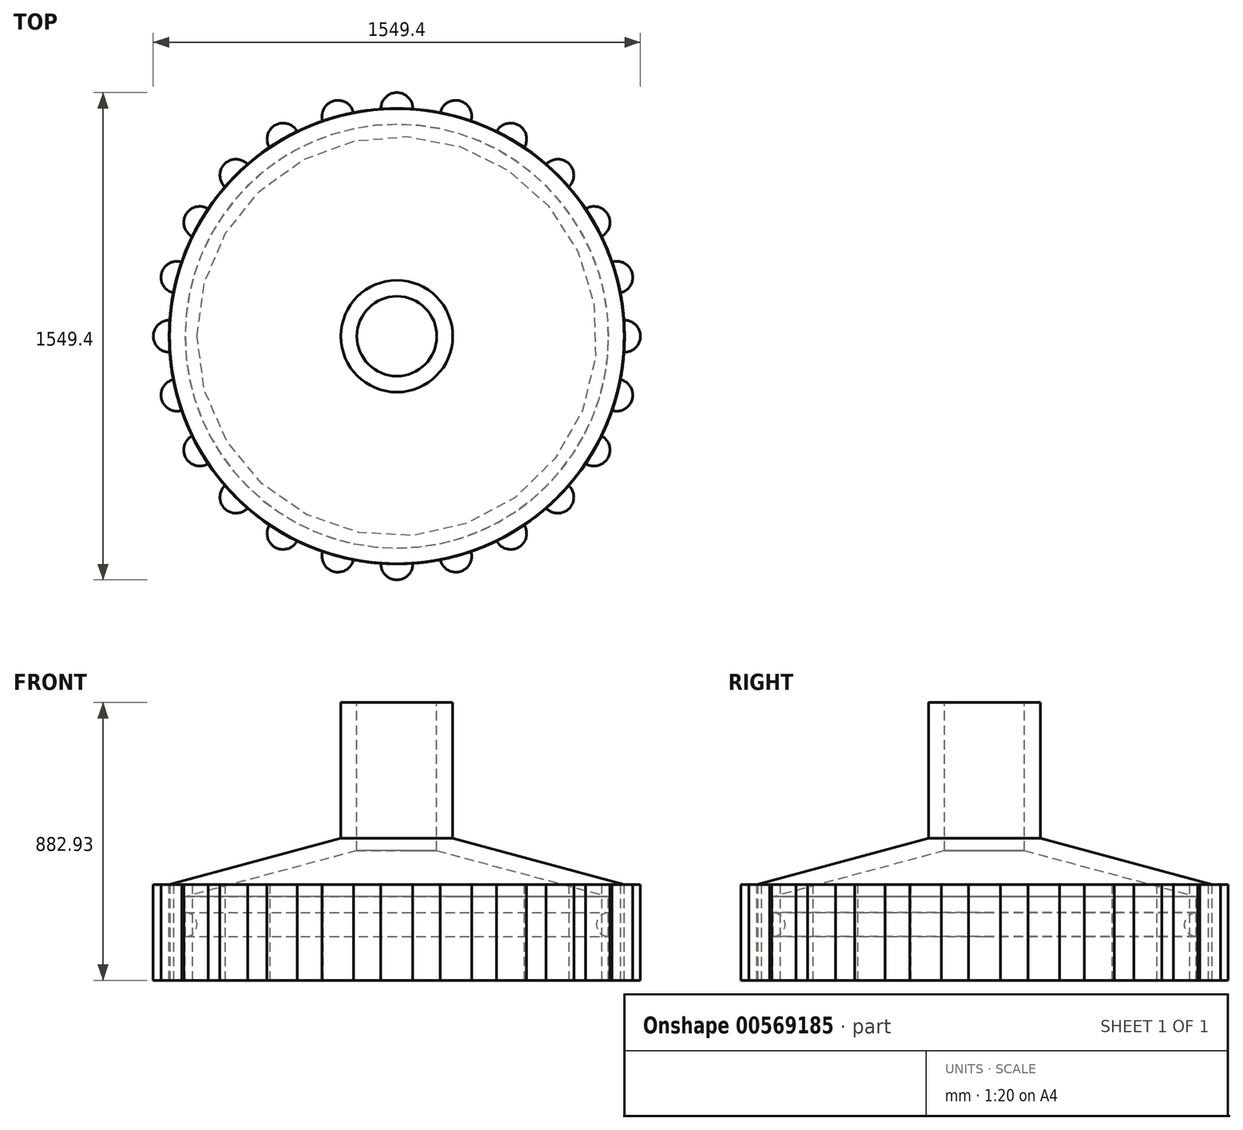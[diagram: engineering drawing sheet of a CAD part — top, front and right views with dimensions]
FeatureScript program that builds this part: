
annotation { "Feature Type Name" : "Feature", "Feature Type Description" : "" }
export const myFeature = defineFeature(function(context is Context, id is Id, definition is map)
    precondition{}
    {
        {
            var Q0;
            Q0=qCreatedBy(makeId("Front.planeOp"),FACE);
            var sketch = newSketch(context, id + "F0", { "sketchPlane" : qUnion([Q0])});
            skLineSegment(sketch, "E0", {"start": v(0, 882.93) * mm, "end": v(0, -770.88) * mm});
            skLineSegment(sketch, "E1", {"start": v(-177.8, 882.93) * mm, "end": v(-177.8, 451.13) * mm});
            skLineSegment(sketch, "E2", {"start": v(-177.8, 451.13) * mm, "end": v(-723.9, 304.8) * mm});
            skLineSegment(sketch, "E3", {"start": v(-723.9, 304.8) * mm, "end": v(-723.9, 0) * mm});
            skLineSegment(sketch, "E4", {"start": v(-723.9, 0) * mm, "end": v(0, 0) * mm});
            skLineSegment(sketch, "E5", {"start": v(-177.8, 882.93) * mm, "end": v(0, 882.93) * mm});
            skSolve(sketch);
        }
        {
            var Q0;
            Q0 = qSketchRegion(id + "F0", true);
            var Q1;
            Q1=sQuery(id+"F0.wireOp",EDGE,"E0");
            revolve(context, id + "F1", {"entities" : qUnion([Q0]), "axis" : qUnion([Q1]), "revolveType" : RevolveType.FULL});
        }
        {
            var Q0;
            Q0=makeQuery(id+"F1.opRevolve","SWEPT_FACE",FACE,{"disambiguationData":[OSD([sQuery(id+"F0.wireOp",EDGE,"E5")])]});
            var Q1;
            Q1=makeQuery(id+"F1.opRevolve","SWEPT_FACE",FACE,{"disambiguationData":[OSD([sQuery(id+"F0.wireOp",EDGE,"E4")])]});
            shell(context, id + "F2", {"entities" : qUnion([Q0, Q1]), "thickness" : 50.8 * mm});
        }
        {
            var Q0;
            Q0=makeQuery(id+"F1.opRevolve","SWEPT_FACE",FACE,{"disambiguationData":[OSD([sQuery(id+"F0.wireOp",EDGE,"E4")])]});
            var sketch = newSketch(context, id + "F3", { "sketchPlane" : qUnion([Q0])});
            skLineSegment(sketch, "E6", {"start": v(0, 0) * mm, "end": v(-892.72, 0) * mm, "construction": true});
            skLineSegment(sketch, "E7", {"start": v(0, 0) * mm, "end": v(0, 820.83) * mm, "construction": true});
            skArc(sketch, "E8", {"start": v(50.77, 722.12) * mm, "mid": v(0, 774.7) * mm, "end": v(-50.77, 722.12) * mm});
            skArc(sketch, "E9", {"start": v(50.77, 722.12) * mm, "mid": v(0, 723.9) * mm, "end": v(-50.77, 722.12) * mm});
            skSolve(sketch);
        }
        {
            var Q0;
            Q0=makeQuery(id+"F3.imprint","IMPRINT",FACE,{"disambiguationData":[TD([[makeQuery(id+"F3.imprint","IMPRINT",EDGE,{"derivedFrom":sQuery(id+"F3.wireOp",EDGE,"E8")}),1.0]])]});
            extrude(context, id + "F4", {"entities" : qUnion([Q0]), "operationType" : NewBodyOperationType.ADD, "oppositeDirection" : true, "depth" : 304.8 * mm, "offsetDistance" : 25.4 * mm});
        }
        {
            var Q0;
            Q0=makeQuery(id+"F1.opRevolve","SWEPT_BODY",BODY,{"disambiguationData":[OSD([sQuery(id+"F0.wireOp",EDGE,"E0"),sQuery(id+"F0.wireOp",EDGE,"E1"),sQuery(id+"F0.wireOp",EDGE,"E2"),sQuery(id+"F0.wireOp",EDGE,"E3"),sQuery(id+"F0.wireOp",EDGE,"E4"),sQuery(id+"F0.wireOp",EDGE,"E5")])]});
            var Q1;
            Q1=makeQuery(id+"F1.opRevolve","SWEPT_FACE",FACE,{"disambiguationData":[OSD([sQuery(id+"F0.wireOp",EDGE,"E3")])]});
            circularPattern(context, id + "F5", {"entities" : qUnion([Q0]), "axis" : qUnion([Q1]), "angle" : 360 * degree, "instanceCount" : 24, "equalSpace" : true});
        }
        {
            var Q0;
            Q0=qCreatedBy(makeId("Front.planeOp"),FACE);
            var sketch = newSketch(context, id + "F6", { "sketchPlane" : qUnion([Q0])});
            skLineSegment(sketch, "E10", {"start": v(0, 0) * mm, "end": v(0, 752.34) * mm, "construction": true});
            skArc(sketch, "E11", {"start": v(-673.87, 138.85) * mm, "mid": v(-635.64, 177.07) * mm, "end": v(-673.87, 215.3) * mm});
            skLineSegment(sketch, "E12", {"start": v(-673.87, 215.3) * mm, "end": v(-673.87, 138.85) * mm});
            skSolve(sketch);
        }
        {
            var Q0;
            Q0 = qSketchRegion(id + "F6", true);
            var Q1;
            Q1=sQuery(id+"F6.wireOp",EDGE,"E10");
            revolve(context, id + "F7", {"entities" : qUnion([Q0]), "axis" : qUnion([Q1]), "revolveType" : RevolveType.FULL});
        }
    });
